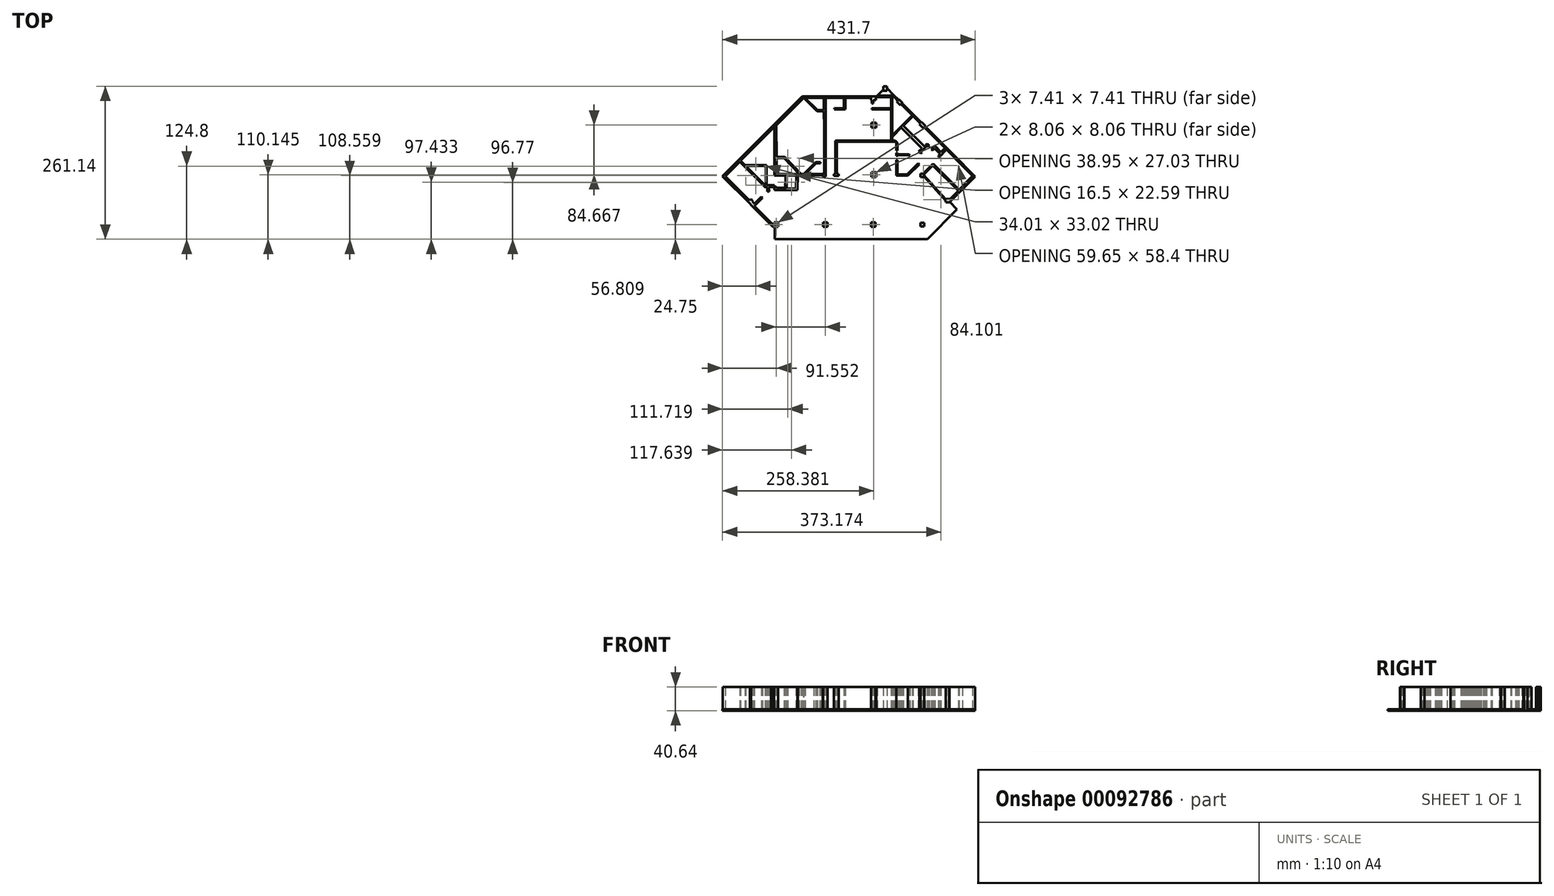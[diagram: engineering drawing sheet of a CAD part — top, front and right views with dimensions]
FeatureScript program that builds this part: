
annotation { "Feature Type Name" : "Feature", "Feature Type Description" : "" }
export const myFeature = defineFeature(function(context is Context, id is Id, definition is map)
    precondition{}
    {
        {
            var Q0;
            Q0=qCreatedBy(makeId("Top.planeOp"),FACE);
            var sketch = newSketch(context, id + "F0", { "sketchPlane" : qUnion([Q0])});
            skLineSegment(sketch, "E0", {"start": v(-215.85, -23.07) * mm, "end": v(-79.78, 113.2) * mm});
            skLineSegment(sketch, "E1", {"start": v(-79.78, 113.2) * mm, "end": v(46.96, 113.2) * mm});
            skLineSegment(sketch, "E2", {"start": v(46.96, 113.2) * mm, "end": v(58.85, 125.1) * mm});
            skLineSegment(sketch, "E3", {"start": v(58.85, 125.1) * mm, "end": v(58.85, 130.59) * mm});
            skLineSegment(sketch, "E4", {"start": v(58.85, 130.59) * mm, "end": v(65.02, 130.59) * mm});
            skLineSegment(sketch, "E5", {"start": v(65.02, 130.59) * mm, "end": v(65.02, 127.13) * mm});
            skLineSegment(sketch, "E6", {"start": v(65.02, 127.13) * mm, "end": v(84.8, 107.35) * mm});
            skLineSegment(sketch, "E7", {"start": v(84.8, 107.35) * mm, "end": v(85.59, 108.14) * mm});
            skLineSegment(sketch, "E8", {"start": v(85.59, 108.14) * mm, "end": v(91.7, 102.02) * mm});
            skLineSegment(sketch, "E9", {"start": v(91.7, 102.02) * mm, "end": v(90.95, 101.28) * mm});
            skLineSegment(sketch, "E10", {"start": v(90.95, 101.28) * mm, "end": v(123.63, 68.6) * mm});
            skLineSegment(sketch, "E11", {"start": v(123.63, 68.6) * mm, "end": v(124.34, 69.31) * mm});
            skLineSegment(sketch, "E12", {"start": v(124.34, 69.31) * mm, "end": v(130.43, 63.22) * mm});
            skLineSegment(sketch, "E13", {"start": v(130.43, 63.22) * mm, "end": v(129.76, 62.54) * mm});
            skLineSegment(sketch, "E14", {"start": v(129.76, 62.54) * mm, "end": v(215.85, -23.56) * mm});
            skLineSegment(sketch, "E15", {"start": v(215.85, -23.56) * mm, "end": v(172.3, -67.15) * mm});
            skLineSegment(sketch, "E16", {"start": v(172.3, -67.15) * mm, "end": v(184.3, -79.94) * mm});
            skLineSegment(sketch, "E17", {"start": v(184.3, -79.94) * mm, "end": v(134.66, -130.59) * mm});
            skLineSegment(sketch, "E18", {"start": v(134.66, -130.59) * mm, "end": v(-126.45, -130.35) * mm});
            skLineSegment(sketch, "E19", {"start": v(-126.45, -130.35) * mm, "end": v(-126.52, -109.63) * mm});
            skLineSegment(sketch, "E20", {"start": v(-126.52, -109.63) * mm, "end": v(-129.44, -109.56) * mm});
            skLineSegment(sketch, "E21", {"start": v(-129.44, -109.56) * mm, "end": v(-132.8, -106.33) * mm});
            skLineSegment(sketch, "E22", {"start": v(-132.8, -106.33) * mm, "end": v(-167.08, -72.04) * mm});
            skLineSegment(sketch, "E23", {"start": v(-167.08, -72.04) * mm, "end": v(-168.6, -70.28) * mm});
            skLineSegment(sketch, "E24", {"start": v(-168.6, -70.28) * mm, "end": v(-215.85, -23.07) * mm});
            skFitSpline(sketch, "E25", {"points": [v(-186.3, 1.77) * mm, v(-171.85, -12.85) * mm, v(-157.2, -27.26) * mm, v(-142.79, -41.93) * mm]});
            skLineSegment(sketch, "E26", {"start": v(-126.77, 61.2) * mm, "end": v(-126.8, -38.64) * mm});
            skLineSegment(sketch, "E27", {"start": v(-126.8, -38.64) * mm, "end": v(-140.51, -38.64) * mm});
            skLineSegment(sketch, "E28", {"start": v(-140.51, -38.64) * mm, "end": v(-140.51, -4.42) * mm});
            skLineSegment(sketch, "E29", {"start": v(-140.51, -4.42) * mm, "end": v(-177.03, -4.42) * mm});
            skLineSegment(sketch, "E30", {"start": v(-177.03, -4.42) * mm, "end": v(-184.77, 3.3) * mm});
            skLineSegment(sketch, "E31", {"start": v(-184.77, 3.3) * mm, "end": v(-186.3, 1.77) * mm});
            skFitSpline(sketch, "E32", {"points": [v(-56.02, -1.5) * mm, v(-56.02, -1.5) * mm, v(-50.03, -1.35) * mm, v(-49.46, -1.5) * mm, v(-56.02, -1.5) * mm]});
            skFitSpline(sketch, "E33", {"points": [v(-49.46, -1.5) * mm, v(-48.9, -1.64) * mm, v(-49.32, 0.79) * mm, v(-49.32, 0.79) * mm, v(-49.46, -1.5) * mm]});
            skLineSegment(sketch, "E34", {"start": v(-142.79, -41.93) * mm, "end": v(-139.28, -41.93) * mm});
            skLineSegment(sketch, "E35", {"start": v(-139.28, -41.93) * mm, "end": v(-139.29, -49.25) * mm});
            skLineSegment(sketch, "E36", {"start": v(-139.29, -49.25) * mm, "end": v(-136.12, -49.48) * mm});
            skLineSegment(sketch, "E37", {"start": v(-136.12, -49.48) * mm, "end": v(-136.52, -41.93) * mm});
            skLineSegment(sketch, "E38", {"start": v(-136.52, -41.93) * mm, "end": v(-126.8, -41.93) * mm});
            skLineSegment(sketch, "E39", {"start": v(-126.8, -41.93) * mm, "end": v(-126.8, -47.66) * mm});
            skLineSegment(sketch, "E40", {"start": v(-126.8, -47.66) * mm, "end": v(-123.39, -47.66) * mm});
            skLineSegment(sketch, "E41", {"start": v(-123.39, -47.66) * mm, "end": v(-123.39, -46.49) * mm});
            skLineSegment(sketch, "E42", {"start": v(-123.39, -46.49) * mm, "end": v(-87.44, -46.72) * mm});
            skLineSegment(sketch, "E43", {"start": v(-87.44, -46.72) * mm, "end": v(-86.94, -21.61) * mm});
            skLineSegment(sketch, "E44", {"start": v(-86.94, -21.61) * mm, "end": v(-44.03, -21.54) * mm});
            skLineSegment(sketch, "E45", {"start": v(-44.03, -21.54) * mm, "end": v(-44.76, -19.22) * mm});
            skLineSegment(sketch, "E46", {"start": v(-44.76, -19.22) * mm, "end": v(-74.5, -19.31) * mm});
            skLineSegment(sketch, "E47", {"start": v(-74.5, -19.31) * mm, "end": v(-56.02, -1.5) * mm});
            skLineSegment(sketch, "E48", {"start": v(-49.32, 0.79) * mm, "end": v(-55.87, 1.07) * mm});
            skLineSegment(sketch, "E49", {"start": v(-55.87, 1.07) * mm, "end": v(-76.69, -19.32) * mm});
            skLineSegment(sketch, "E50", {"start": v(-76.69, -19.32) * mm, "end": v(-81.21, -19.34) * mm});
            skLineSegment(sketch, "E51", {"start": v(-81.21, -19.34) * mm, "end": v(-109.05, 9.62) * mm});
            skLineSegment(sketch, "E52", {"start": v(-109.05, 9.62) * mm, "end": v(-123.39, 9.48) * mm});
            skLineSegment(sketch, "E53", {"start": v(-123.39, 9.48) * mm, "end": v(-123.39, 31.81) * mm});
            skLineSegment(sketch, "E54", {"start": v(-123.39, 31.81) * mm, "end": v(-123.46, 64.51) * mm});
            skLineSegment(sketch, "E55", {"start": v(-123.46, 64.51) * mm, "end": v(-126.77, 61.2) * mm});
            skLineSegment(sketch, "E56", {"start": v(-8.23, 111.03) * mm, "end": v(-8.44, 93.23) * mm});
            skLineSegment(sketch, "E57", {"start": v(-8.44, 93.23) * mm, "end": v(-24.56, 93.56) * mm});
            skLineSegment(sketch, "E58", {"start": v(-24.56, 93.56) * mm, "end": v(-24.7, 91.44) * mm});
            skLineSegment(sketch, "E59", {"start": v(-24.7, 91.44) * mm, "end": v(-6.21, 91.4) * mm});
            skLineSegment(sketch, "E60", {"start": v(-6.21, 91.4) * mm, "end": v(-5.91, 111.02) * mm});
            skLineSegment(sketch, "E61", {"start": v(-5.91, 111.02) * mm, "end": v(37.7, 110.88) * mm});
            skLineSegment(sketch, "E62", {"start": v(37.7, 110.88) * mm, "end": v(37.7, 107.03) * mm});
            skLineSegment(sketch, "E63", {"start": v(37.7, 107.03) * mm, "end": v(39.2, 107.03) * mm});
            skLineSegment(sketch, "E64", {"start": v(39.2, 107.03) * mm, "end": v(39.2, 101.13) * mm});
            skLineSegment(sketch, "E65", {"start": v(39.2, 101.13) * mm, "end": v(41.9, 101.13) * mm});
            skLineSegment(sketch, "E66", {"start": v(41.9, 101.13) * mm, "end": v(41.9, 107) * mm});
            skLineSegment(sketch, "E67", {"start": v(41.9, 107) * mm, "end": v(46.12, 106.98) * mm});
            skLineSegment(sketch, "E68", {"start": v(46.12, 106.98) * mm, "end": v(46.1, 111.97) * mm});
            skLineSegment(sketch, "E69", {"start": v(46.1, 111.97) * mm, "end": v(72.04, 112.1) * mm});
            skLineSegment(sketch, "E70", {"start": v(72.04, 112.1) * mm, "end": v(71.96, 93.06) * mm});
            skLineSegment(sketch, "E71", {"start": v(71.96, 93.06) * mm, "end": v(39.07, 93.1) * mm});
            skLineSegment(sketch, "E72", {"start": v(39.07, 93.1) * mm, "end": v(39.39, 91.15) * mm});
            skLineSegment(sketch, "E73", {"start": v(39.39, 91.15) * mm, "end": v(72.19, 91.01) * mm});
            skLineSegment(sketch, "E74", {"start": v(72.19, 91.01) * mm, "end": v(72.26, 80.52) * mm});
            skLineSegment(sketch, "E75", {"start": v(72.26, 80.52) * mm, "end": v(73.98, 80.49) * mm});
            skLineSegment(sketch, "E76", {"start": v(73.98, 80.49) * mm, "end": v(74.27, 112.15) * mm});
            skLineSegment(sketch, "E77", {"start": v(74.27, 112.15) * mm, "end": v(77.66, 112.2) * mm});
            skLineSegment(sketch, "E78", {"start": v(77.66, 112.2) * mm, "end": v(83.4, 105.92) * mm});
            skLineSegment(sketch, "E79", {"start": v(83.4, 105.92) * mm, "end": v(84.97, 107.56) * mm});
            skLineSegment(sketch, "E80", {"start": v(84.97, 107.56) * mm, "end": v(77.56, 114.78) * mm});
            skLineSegment(sketch, "E81", {"start": v(77.56, 114.78) * mm, "end": v(46.1, 114.8) * mm});
            skLineSegment(sketch, "E82", {"start": v(46.1, 114.8) * mm, "end": v(37.7, 114.8) * mm});
            skLineSegment(sketch, "E83", {"start": v(37.7, 114.8) * mm, "end": v(-78.2, 114.88) * mm});
            skLineSegment(sketch, "E84", {"start": v(-78.2, 114.88) * mm, "end": v(-215.75, -23.11) * mm});
            skLineSegment(sketch, "E85", {"start": v(-215.75, -23.11) * mm, "end": v(-169.21, -69.65) * mm});
            skLineSegment(sketch, "E86", {"start": v(-169.21, -69.65) * mm, "end": v(-169.36, -69.8) * mm});
            skLineSegment(sketch, "E87", {"start": v(-169.36, -69.8) * mm, "end": v(-129.37, -109.8) * mm});
            skLineSegment(sketch, "E88", {"start": v(-129.37, -109.8) * mm, "end": v(-126.86, -109.12) * mm});
            skLineSegment(sketch, "E89", {"start": v(-126.86, -109.12) * mm, "end": v(-126.86, -105.06) * mm});
            skLineSegment(sketch, "E90", {"start": v(-126.86, -105.06) * mm, "end": v(-130.35, -105.06) * mm});
            skLineSegment(sketch, "E91", {"start": v(-130.35, -105.06) * mm, "end": v(-161.43, -73.98) * mm});
            skLineSegment(sketch, "E92", {"start": v(-161.43, -73.98) * mm, "end": v(-147.4, -59.94) * mm});
            skLineSegment(sketch, "E93", {"start": v(-147.4, -59.94) * mm, "end": v(-149.1, -57.8) * mm});
            skLineSegment(sketch, "E94", {"start": v(-149.1, -57.8) * mm, "end": v(-161.22, -69.92) * mm});
            skLineSegment(sketch, "E95", {"start": v(-161.22, -69.92) * mm, "end": v(-164.83, -66.56) * mm});
            skLineSegment(sketch, "E96", {"start": v(-164.83, -66.56) * mm, "end": v(-163.73, -65.45) * mm});
            skLineSegment(sketch, "E97", {"start": v(-163.73, -65.45) * mm, "end": v(-167.29, -61.88) * mm});
            skLineSegment(sketch, "E98", {"start": v(-167.29, -61.88) * mm, "end": v(-169.86, -64.45) * mm});
            skLineSegment(sketch, "E99", {"start": v(-169.86, -64.45) * mm, "end": v(-211.2, -23.11) * mm});
            skLineSegment(sketch, "E100", {"start": v(-211.2, -23.11) * mm, "end": v(-76.8, 111.13) * mm});
            skLineSegment(sketch, "E101", {"start": v(-76.8, 111.13) * mm, "end": v(-8.23, 111.03) * mm});
            skFitSpline(sketch, "E102", {"points": [v(-42.68, 107.03) * mm, v(-42.64, 102.79) * mm, v(-42.66, 98.54) * mm, v(-42.8, 94.3) * mm]});
            skLineSegment(sketch, "E103", {"start": v(-45.39, 111.13) * mm, "end": v(-45.48, 107.13) * mm});
            skLineSegment(sketch, "E104", {"start": v(-45.48, 107.13) * mm, "end": v(-42.68, 107.03) * mm});
            skFitSpline(sketch, "E105", {"points": [v(-41.4, -20.44) * mm, v(-41.14, -22.5) * mm, v(-38.06, -19.94) * mm, v(-37.9, -21.46) * mm]});
            skFitSpline(sketch, "E106", {"points": [v(-37.9, -21.46) * mm, v(-37.4, -25.88) * mm, v(-38.04, -19.38) * mm, v(-38.04, -19.38) * mm, v(-37.9, -21.46) * mm]});
            skLineSegment(sketch, "E107", {"start": v(-42.8, 94.3) * mm, "end": v(-42.8, 65.7) * mm});
            skLineSegment(sketch, "E108", {"start": v(-42.8, 65.7) * mm, "end": v(-44.13, 65.7) * mm});
            skLineSegment(sketch, "E109", {"start": v(-44.13, 65.7) * mm, "end": v(-44.13, 60.85) * mm});
            skLineSegment(sketch, "E110", {"start": v(-44.13, 60.85) * mm, "end": v(-42.18, 60.85) * mm});
            skLineSegment(sketch, "E111", {"start": v(-42.18, 60.85) * mm, "end": v(-41.4, -20.44) * mm});
            skLineSegment(sketch, "E112", {"start": v(-38.04, -19.38) * mm, "end": v(-39.19, -19.31) * mm});
            skLineSegment(sketch, "E113", {"start": v(-39.19, -19.31) * mm, "end": v(-39.19, 60.64) * mm});
            skLineSegment(sketch, "E114", {"start": v(-39.19, 60.64) * mm, "end": v(-39.28, 62.96) * mm});
            skLineSegment(sketch, "E115", {"start": v(-39.28, 62.96) * mm, "end": v(-39.28, 65.7) * mm});
            skLineSegment(sketch, "E116", {"start": v(-39.28, 65.7) * mm, "end": v(-39.58, 65.7) * mm});
            skLineSegment(sketch, "E117", {"start": v(-39.58, 65.7) * mm, "end": v(-39.58, 90.87) * mm});
            skLineSegment(sketch, "E118", {"start": v(-39.58, 90.87) * mm, "end": v(-31.65, 90.87) * mm});
            skLineSegment(sketch, "E119", {"start": v(-31.65, 90.87) * mm, "end": v(-31.69, 93.32) * mm});
            skLineSegment(sketch, "E120", {"start": v(-31.69, 93.32) * mm, "end": v(-39.56, 93.3) * mm});
            skLineSegment(sketch, "E121", {"start": v(-39.56, 93.3) * mm, "end": v(-39.58, 107.03) * mm});
            skLineSegment(sketch, "E122", {"start": v(-39.58, 107.03) * mm, "end": v(-39.53, 111.09) * mm});
            skLineSegment(sketch, "E123", {"start": v(-39.53, 111.09) * mm, "end": v(-45.39, 111.13) * mm});
            skLineSegment(sketch, "E124", {"start": v(-110.62, 7.62) * mm, "end": v(-84.44, -19.35) * mm});
            skLineSegment(sketch, "E125", {"start": v(-84.44, -19.35) * mm, "end": v(-89, -19.37) * mm});
            skLineSegment(sketch, "E126", {"start": v(-89, -19.37) * mm, "end": v(-100.11, -19.4) * mm});
            skLineSegment(sketch, "E127", {"start": v(-100.11, -19.4) * mm, "end": v(-103.15, -19.4) * mm});
            skLineSegment(sketch, "E128", {"start": v(-103.15, -19.4) * mm, "end": v(-123.39, -19.4) * mm});
            skLineSegment(sketch, "E129", {"start": v(-123.39, -19.4) * mm, "end": v(-123.39, 7.49) * mm});
            skLineSegment(sketch, "E130", {"start": v(-123.39, 7.49) * mm, "end": v(-110.62, 7.62) * mm});
            skLineSegment(sketch, "E131", {"start": v(-175.83, -5.62) * mm, "end": v(-141.82, -5.62) * mm});
            skLineSegment(sketch, "E132", {"start": v(-141.82, -5.62) * mm, "end": v(-141.82, -38.64) * mm});
            skLineSegment(sketch, "E133", {"start": v(-141.82, -38.64) * mm, "end": v(-142.77, -38.64) * mm});
            skLineSegment(sketch, "E134", {"start": v(-142.77, -38.64) * mm, "end": v(-175.83, -5.62) * mm});
            skFitSpline(sketch, "E135", {"points": [v(-89.96, -44.54) * mm, v(-95.39, -44.46) * mm, v(-100.81, -44.51) * mm, v(-106.24, -44.55) * mm]});
            skLineSegment(sketch, "E136", {"start": v(-89.74, -21.97) * mm, "end": v(-89.96, -44.54) * mm});
            skLineSegment(sketch, "E137", {"start": v(-106.24, -44.55) * mm, "end": v(-106.13, -43.27) * mm});
            skLineSegment(sketch, "E138", {"start": v(-106.13, -43.27) * mm, "end": v(-106.13, -40.36) * mm});
            skLineSegment(sketch, "E139", {"start": v(-106.13, -40.36) * mm, "end": v(-106.13, -29.97) * mm});
            skLineSegment(sketch, "E140", {"start": v(-106.13, -29.97) * mm, "end": v(-106.13, -22.12) * mm});
            skLineSegment(sketch, "E141", {"start": v(-106.13, -22.12) * mm, "end": v(-104.14, -22.12) * mm});
            skLineSegment(sketch, "E142", {"start": v(-104.14, -22.12) * mm, "end": v(-89.74, -21.97) * mm});
            skLineSegment(sketch, "E143", {"start": v(-123.39, -22.12) * mm, "end": v(-108.2, -22.12) * mm});
            skLineSegment(sketch, "E144", {"start": v(-108.2, -22.12) * mm, "end": v(-108.2, -29.05) * mm});
            skLineSegment(sketch, "E145", {"start": v(-108.2, -29.05) * mm, "end": v(-108.41, -40.15) * mm});
            skLineSegment(sketch, "E146", {"start": v(-108.41, -40.15) * mm, "end": v(-108.38, -42.92) * mm});
            skLineSegment(sketch, "E147", {"start": v(-108.38, -42.92) * mm, "end": v(-123.39, -42.92) * mm});
            skLineSegment(sketch, "E148", {"start": v(-123.39, -42.92) * mm, "end": v(-123.39, -22.12) * mm});
            skLineSegment(sketch, "E149", {"start": v(-44.13, -19.12) * mm, "end": v(-39.28, -19.12) * mm});
            skLineSegment(sketch, "E150", {"start": v(-39.28, -19.12) * mm, "end": v(-39.28, -23.97) * mm});
            skLineSegment(sketch, "E151", {"start": v(-39.28, -23.97) * mm, "end": v(-44.13, -23.97) * mm});
            skLineSegment(sketch, "E152", {"start": v(-44.13, -23.97) * mm, "end": v(-44.13, -19.12) * mm});
            skLineSegment(sketch, "E153", {"start": v(90.99, 101.49) * mm, "end": v(89.12, 100.4) * mm});
            skLineSegment(sketch, "E154", {"start": v(89.12, 100.4) * mm, "end": v(108.5, 80.9) * mm});
            skLineSegment(sketch, "E155", {"start": v(108.5, 80.9) * mm, "end": v(75.07, 47.74) * mm});
            skLineSegment(sketch, "E156", {"start": v(75.07, 47.74) * mm, "end": v(75.12, 45.54) * mm});
            skLineSegment(sketch, "E157", {"start": v(75.12, 45.54) * mm, "end": v(89.59, 59.7) * mm});
            skLineSegment(sketch, "E158", {"start": v(89.59, 59.7) * mm, "end": v(124.84, 24.66) * mm});
            skLineSegment(sketch, "E159", {"start": v(124.84, 24.66) * mm, "end": v(119.4, 19.21) * mm});
            skLineSegment(sketch, "E160", {"start": v(119.4, 19.21) * mm, "end": v(122.82, 15.38) * mm});
            skLineSegment(sketch, "E161", {"start": v(122.82, 15.38) * mm, "end": v(124.63, 17) * mm});
            skLineSegment(sketch, "E162", {"start": v(124.63, 17) * mm, "end": v(122.82, 19.02) * mm});
            skLineSegment(sketch, "E163", {"start": v(122.82, 19.02) * mm, "end": v(133.5, 29.3) * mm});
            skLineSegment(sketch, "E164", {"start": v(133.5, 29.3) * mm, "end": v(135.52, 27.08) * mm});
            skLineSegment(sketch, "E165", {"start": v(135.52, 27.08) * mm, "end": v(137.33, 28.9) * mm});
            skLineSegment(sketch, "E166", {"start": v(137.33, 28.9) * mm, "end": v(134.1, 32.52) * mm});
            skLineSegment(sketch, "E167", {"start": v(134.1, 32.52) * mm, "end": v(129.07, 27.48) * mm});
            skLineSegment(sketch, "E168", {"start": v(129.07, 27.48) * mm, "end": v(93.04, 63.1) * mm});
            skLineSegment(sketch, "E169", {"start": v(93.04, 63.1) * mm, "end": v(109.8, 79.59) * mm});
            skLineSegment(sketch, "E170", {"start": v(109.8, 79.59) * mm, "end": v(122.15, 67.16) * mm});
            skLineSegment(sketch, "E171", {"start": v(122.15, 67.16) * mm, "end": v(120.57, 65.58) * mm});
            skLineSegment(sketch, "E172", {"start": v(120.57, 65.58) * mm, "end": v(126.7, 59.45) * mm});
            skLineSegment(sketch, "E173", {"start": v(126.7, 59.45) * mm, "end": v(128.26, 61.02) * mm});
            skLineSegment(sketch, "E174", {"start": v(128.26, 61.02) * mm, "end": v(159.59, 29.49) * mm});
            skLineSegment(sketch, "E175", {"start": v(159.59, 29.49) * mm, "end": v(164.15, 24.87) * mm});
            skLineSegment(sketch, "E176", {"start": v(164.15, 24.87) * mm, "end": v(157.3, 18.2) * mm});
            skLineSegment(sketch, "E177", {"start": v(157.3, 18.2) * mm, "end": v(147.42, 28.7) * mm});
            skLineSegment(sketch, "E178", {"start": v(147.42, 28.7) * mm, "end": v(140.96, 22.64) * mm});
            skLineSegment(sketch, "E179", {"start": v(140.96, 22.64) * mm, "end": v(143.18, 21.03) * mm});
            skLineSegment(sketch, "E180", {"start": v(143.18, 21.03) * mm, "end": v(146.8, 24.66) * mm});
            skLineSegment(sketch, "E181", {"start": v(146.8, 24.66) * mm, "end": v(155.88, 14.98) * mm});
            skLineSegment(sketch, "E182", {"start": v(155.88, 14.98) * mm, "end": v(152.86, 11.56) * mm});
            skLineSegment(sketch, "E183", {"start": v(152.86, 11.56) * mm, "end": v(154.27, 9.33) * mm});
            skLineSegment(sketch, "E184", {"start": v(154.27, 9.33) * mm, "end": v(166.67, 22.32) * mm});
            skLineSegment(sketch, "E185", {"start": v(166.67, 22.32) * mm, "end": v(193.9, -5.21) * mm});
            skLineSegment(sketch, "E186", {"start": v(193.9, -5.21) * mm, "end": v(198.22, -9.5) * mm});
            skLineSegment(sketch, "E187", {"start": v(198.22, -9.5) * mm, "end": v(211.45, -22.82) * mm});
            skLineSegment(sketch, "E188", {"start": v(211.45, -22.82) * mm, "end": v(188.53, -45.74) * mm});
            skLineSegment(sketch, "E189", {"start": v(188.53, -45.74) * mm, "end": v(143.82, -1.7) * mm});
            skLineSegment(sketch, "E190", {"start": v(143.82, -1.7) * mm, "end": v(124.93, -20.23) * mm});
            skLineSegment(sketch, "E191", {"start": v(124.93, -20.23) * mm, "end": v(165.64, -65.01) * mm});
            skLineSegment(sketch, "E192", {"start": v(165.64, -65.01) * mm, "end": v(165.64, -67.71) * mm});
            skLineSegment(sketch, "E193", {"start": v(165.64, -67.71) * mm, "end": v(171.29, -67.71) * mm});
            skLineSegment(sketch, "E194", {"start": v(171.29, -67.71) * mm, "end": v(171.41, -67.9) * mm});
            skLineSegment(sketch, "E195", {"start": v(171.41, -67.9) * mm, "end": v(171.6, -67.71) * mm});
            skLineSegment(sketch, "E196", {"start": v(171.6, -67.71) * mm, "end": v(171.62, -67.71) * mm});
            skLineSegment(sketch, "E197", {"start": v(171.62, -67.71) * mm, "end": v(171.62, -67.69) * mm});
            skLineSegment(sketch, "E198", {"start": v(171.62, -67.69) * mm, "end": v(215.8, -23.57) * mm});
            skLineSegment(sketch, "E199", {"start": v(215.8, -23.57) * mm, "end": v(129.82, 62.58) * mm});
            skLineSegment(sketch, "E200", {"start": v(129.82, 62.58) * mm, "end": v(130.5, 63.24) * mm});
            skLineSegment(sketch, "E201", {"start": v(130.5, 63.24) * mm, "end": v(124.35, 69.37) * mm});
            skLineSegment(sketch, "E202", {"start": v(124.35, 69.37) * mm, "end": v(123.7, 68.71) * mm});
            skLineSegment(sketch, "E203", {"start": v(123.7, 68.71) * mm, "end": v(90.99, 101.49) * mm});
            skLineSegment(sketch, "E204", {"start": v(143.45, -4.62) * mm, "end": v(187.15, -47.77) * mm});
            skLineSegment(sketch, "E205", {"start": v(187.15, -47.77) * mm, "end": v(171.62, -63.02) * mm});
            skLineSegment(sketch, "E206", {"start": v(171.62, -63.02) * mm, "end": v(171.62, -61.58) * mm});
            skLineSegment(sketch, "E207", {"start": v(171.62, -61.58) * mm, "end": v(165.64, -61.58) * mm});
            skLineSegment(sketch, "E208", {"start": v(165.64, -61.58) * mm, "end": v(165.64, -62.48) * mm});
            skLineSegment(sketch, "E209", {"start": v(165.64, -62.48) * mm, "end": v(127.5, -20.46) * mm});
            skLineSegment(sketch, "E210", {"start": v(127.5, -20.46) * mm, "end": v(143.45, -4.62) * mm});
            skLineSegment(sketch, "E211", {"start": v(38.5, 68.25) * mm, "end": v(46.56, 68.25) * mm});
            skLineSegment(sketch, "E212", {"start": v(46.56, 68.25) * mm, "end": v(46.56, 60.2) * mm});
            skLineSegment(sketch, "E213", {"start": v(46.56, 60.2) * mm, "end": v(38.5, 60.2) * mm});
            skLineSegment(sketch, "E214", {"start": v(38.5, 60.2) * mm, "end": v(38.5, 68.25) * mm});
            skLineSegment(sketch, "E215", {"start": v(38.5, -16.41) * mm, "end": v(46.56, -16.41) * mm});
            skLineSegment(sketch, "E216", {"start": v(46.56, -16.41) * mm, "end": v(46.56, -24.48) * mm});
            skLineSegment(sketch, "E217", {"start": v(46.56, -24.48) * mm, "end": v(38.5, -24.48) * mm});
            skLineSegment(sketch, "E218", {"start": v(38.5, -24.48) * mm, "end": v(38.5, -16.41) * mm});
            skLineSegment(sketch, "E219", {"start": v(85.58, 108.14) * mm, "end": v(91.71, 102.01) * mm});
            skLineSegment(sketch, "E220", {"start": v(91.71, 102.01) * mm, "end": v(87.93, 98.22) * mm});
            skLineSegment(sketch, "E221", {"start": v(87.93, 98.22) * mm, "end": v(81.8, 104.35) * mm});
            skLineSegment(sketch, "E222", {"start": v(81.8, 104.35) * mm, "end": v(85.58, 108.14) * mm});
            skLineSegment(sketch, "E223", {"start": v(58.79, 130.55) * mm, "end": v(65.06, 130.55) * mm});
            skLineSegment(sketch, "E224", {"start": v(65.06, 130.55) * mm, "end": v(65.06, 122.85) * mm});
            skLineSegment(sketch, "E225", {"start": v(65.06, 122.85) * mm, "end": v(58.79, 122.85) * mm});
            skLineSegment(sketch, "E226", {"start": v(58.79, 122.85) * mm, "end": v(58.79, 130.55) * mm});
            skLineSegment(sketch, "E227", {"start": v(-43.9, -102.13) * mm, "end": v(-36.5, -102.13) * mm});
            skLineSegment(sketch, "E228", {"start": v(-36.5, -102.13) * mm, "end": v(-36.5, -109.55) * mm});
            skLineSegment(sketch, "E229", {"start": v(-36.5, -109.55) * mm, "end": v(-43.9, -109.55) * mm});
            skLineSegment(sketch, "E230", {"start": v(-43.9, -109.55) * mm, "end": v(-43.9, -102.13) * mm});
            skLineSegment(sketch, "E231", {"start": v(37.92, -102.13) * mm, "end": v(45.33, -102.13) * mm});
            skLineSegment(sketch, "E232", {"start": v(45.33, -102.13) * mm, "end": v(45.33, -109.55) * mm});
            skLineSegment(sketch, "E233", {"start": v(45.33, -109.55) * mm, "end": v(37.92, -109.55) * mm});
            skLineSegment(sketch, "E234", {"start": v(37.92, -109.55) * mm, "end": v(37.92, -102.13) * mm});
            skLineSegment(sketch, "E235", {"start": v(-128, -102.13) * mm, "end": v(-120.6, -102.13) * mm});
            skLineSegment(sketch, "E236", {"start": v(-120.6, -102.13) * mm, "end": v(-120.6, -109.55) * mm});
            skLineSegment(sketch, "E237", {"start": v(-120.6, -109.55) * mm, "end": v(-128, -109.55) * mm});
            skLineSegment(sketch, "E238", {"start": v(-128, -109.55) * mm, "end": v(-128, -102.13) * mm});
            skLineSegment(sketch, "E239", {"start": v(122.45, -18.53) * mm, "end": v(128.43, -18.53) * mm});
            skLineSegment(sketch, "E240", {"start": v(128.43, -18.53) * mm, "end": v(128.43, -24.66) * mm});
            skLineSegment(sketch, "E241", {"start": v(128.43, -24.66) * mm, "end": v(122.45, -24.66) * mm});
            skLineSegment(sketch, "E242", {"start": v(122.45, -24.66) * mm, "end": v(122.45, -18.53) * mm});
            skLineSegment(sketch, "E243", {"start": v(122.45, -102.8) * mm, "end": v(128.43, -102.8) * mm});
            skLineSegment(sketch, "E244", {"start": v(128.43, -102.8) * mm, "end": v(128.43, -108.92) * mm});
            skLineSegment(sketch, "E245", {"start": v(128.43, -108.92) * mm, "end": v(122.45, -108.92) * mm});
            skLineSegment(sketch, "E246", {"start": v(122.45, -108.92) * mm, "end": v(122.45, -102.8) * mm});
            skFitSpline(sketch, "E247", {"points": [v(81.28, 35.54) * mm, v(81.67, 35.54) * mm, v(81.28, 22.99) * mm, v(81.28, 22.99) * mm, v(81.28, 35.54) * mm]});
            skLineSegment(sketch, "E248", {"start": v(72.22, 74.65) * mm, "end": v(72.22, 37.96) * mm});
            skLineSegment(sketch, "E249", {"start": v(72.22, 37.96) * mm, "end": v(-22.53, 37.96) * mm});
            skLineSegment(sketch, "E250", {"start": v(-22.53, 37.96) * mm, "end": v(-22.53, -19.08) * mm});
            skLineSegment(sketch, "E251", {"start": v(-22.53, -19.08) * mm, "end": v(-24.09, -19.08) * mm});
            skLineSegment(sketch, "E252", {"start": v(-24.09, -19.08) * mm, "end": v(-24.14, -21.71) * mm});
            skLineSegment(sketch, "E253", {"start": v(-24.14, -21.71) * mm, "end": v(-17.74, -21.71) * mm});
            skLineSegment(sketch, "E254", {"start": v(-17.74, -21.71) * mm, "end": v(-17.74, -19.08) * mm});
            skLineSegment(sketch, "E255", {"start": v(-17.74, -19.08) * mm, "end": v(-20.3, -19.08) * mm});
            skLineSegment(sketch, "E256", {"start": v(-20.3, -19.08) * mm, "end": v(-20.3, 35.54) * mm});
            skLineSegment(sketch, "E257", {"start": v(-20.3, 35.54) * mm, "end": v(81.28, 35.54) * mm});
            skFitSpline(sketch, "E258", {"points": [v(83.53, 12.76) * mm, v(83.53, 12.76) * mm, v(99.18, 12.86) * mm, v(104.5, 12.8) * mm, v(83.53, 12.76) * mm]});
            skLineSegment(sketch, "E259", {"start": v(81.28, 22.99) * mm, "end": v(83.3, 22.44) * mm});
            skLineSegment(sketch, "E260", {"start": v(83.3, 22.44) * mm, "end": v(83.3, 33.67) * mm});
            skLineSegment(sketch, "E261", {"start": v(83.3, 33.67) * mm, "end": v(102.82, 14.47) * mm});
            skLineSegment(sketch, "E262", {"start": v(102.82, 14.47) * mm, "end": v(83.68, 14.47) * mm});
            skLineSegment(sketch, "E263", {"start": v(83.68, 14.47) * mm, "end": v(83.68, 16.32) * mm});
            skLineSegment(sketch, "E264", {"start": v(83.68, 16.32) * mm, "end": v(81.82, 16.32) * mm});
            skLineSegment(sketch, "E265", {"start": v(81.82, 16.32) * mm, "end": v(81.82, 11.04) * mm});
            skLineSegment(sketch, "E266", {"start": v(81.82, 11.04) * mm, "end": v(83.53, 11.04) * mm});
            skLineSegment(sketch, "E267", {"start": v(83.53, 11.04) * mm, "end": v(83.53, 12.76) * mm});
            skLineSegment(sketch, "E268", {"start": v(104.5, 12.8) * mm, "end": v(118.67, -1.14) * mm});
            skLineSegment(sketch, "E269", {"start": v(118.67, -1.14) * mm, "end": v(99.48, -20.34) * mm});
            skLineSegment(sketch, "E270", {"start": v(99.48, -20.34) * mm, "end": v(83.5, -20.34) * mm});
            skLineSegment(sketch, "E271", {"start": v(83.5, -20.34) * mm, "end": v(83.5, 4.75) * mm});
            skLineSegment(sketch, "E272", {"start": v(83.5, 4.75) * mm, "end": v(81.3, 4.7) * mm});
            skLineSegment(sketch, "E273", {"start": v(81.3, 4.7) * mm, "end": v(81.3, -22.1) * mm});
            skLineSegment(sketch, "E274", {"start": v(81.3, -22.1) * mm, "end": v(101.05, -22.1) * mm});
            skLineSegment(sketch, "E275", {"start": v(101.05, -22.1) * mm, "end": v(132.8, 9.64) * mm});
            skLineSegment(sketch, "E276", {"start": v(132.8, 9.64) * mm, "end": v(129.48, 12.97) * mm});
            skLineSegment(sketch, "E277", {"start": v(129.48, 12.97) * mm, "end": v(126.85, 10.35) * mm});
            skLineSegment(sketch, "E278", {"start": v(126.85, 10.35) * mm, "end": v(128.95, 9.13) * mm});
            skLineSegment(sketch, "E279", {"start": v(128.95, 9.13) * mm, "end": v(120.1, 0.28) * mm});
            skLineSegment(sketch, "E280", {"start": v(120.1, 0.28) * mm, "end": v(75.12, 45.25) * mm});
            skLineSegment(sketch, "E281", {"start": v(75.12, 45.25) * mm, "end": v(75.04, 45.18) * mm});
            skLineSegment(sketch, "E282", {"start": v(75.04, 45.18) * mm, "end": v(75.04, 74.65) * mm});
            skLineSegment(sketch, "E283", {"start": v(75.04, 74.65) * mm, "end": v(72.22, 74.65) * mm});
            skLineSegment(sketch, "E284", {"start": v(75.04, 41.8) * mm, "end": v(79.36, 37.56) * mm});
            skLineSegment(sketch, "E285", {"start": v(79.36, 37.56) * mm, "end": v(75.04, 37.56) * mm});
            skLineSegment(sketch, "E286", {"start": v(75.04, 37.56) * mm, "end": v(75.04, 41.8) * mm});
            skLineSegment(sketch, "E287", {"start": v(-49.32, 89.73) * mm, "end": v(-49.32, 87.6) * mm});
            skLineSegment(sketch, "E288", {"start": v(-49.32, 87.6) * mm, "end": v(-53.74, 87.6) * mm});
            skLineSegment(sketch, "E289", {"start": v(-53.74, 87.6) * mm, "end": v(-76.79, 111) * mm});
            skLineSegment(sketch, "E290", {"start": v(-76.79, 111) * mm, "end": v(-74.76, 111.08) * mm});
            skLineSegment(sketch, "E291", {"start": v(-74.76, 111.08) * mm, "end": v(-53.38, 89.8) * mm});
            skLineSegment(sketch, "E292", {"start": v(-53.38, 89.8) * mm, "end": v(-49.32, 89.73) * mm});
            skLineSegment(sketch, "E293", {"start": v(-59.62, 93.4) * mm, "end": v(-81.8, 70.01) * mm});
            skLineSegment(sketch, "E294", {"start": v(-81.8, 70.01) * mm, "end": v(-81.8, 20.02) * mm});
            skLineSegment(sketch, "E295", {"start": v(-81.8, 20.02) * mm, "end": v(-59.11, -2.66) * mm});
            skLineSegment(sketch, "E296", {"start": v(-59.11, -2.66) * mm, "end": v(-67.68, -11.22) * mm});
            skLineSegment(sketch, "E297", {"start": v(-67.68, -11.22) * mm, "end": v(-94.8, 15.89) * mm});
            skLineSegment(sketch, "E298", {"start": v(-94.8, 15.89) * mm, "end": v(-94.8, 74.65) * mm});
            skLineSegment(sketch, "E299", {"start": v(-94.8, 74.65) * mm, "end": v(-67.37, 101) * mm});
            skLineSegment(sketch, "E300", {"start": v(-67.37, 101) * mm, "end": v(-59.62, 93.4) * mm});
            skSolve(sketch);
        }
        {
            var Q0;
            {var subQ26=sQuery(id+"F0.wireOp",EDGE,"E1");Q0=makeQuery(id+"F0.imprint","IMPRINT",FACE,{"disambiguationData":[TD([[makeQuery(id+"F0.imprint","IMPRINT",EDGE,{"derivedFrom":subQ26}),-1.0]])]});}
            var Q1;
            {var subQ16=sQuery(id+"F0.wireOp",EDGE,"E11");Q1=makeQuery(id+"F0.imprint","IMPRINT",FACE,{"disambiguationData":[TD([[makeQuery(id+"F0.imprint","IMPRINT",EDGE,{"derivedFrom":subQ16}),-1.0]])]});}
            var Q2;
            Q2=makeQuery(id+"F0.imprint","IMPRINT",FACE,{"disambiguationData":[TD([[makeQuery(id+"F0.imprint","IMPRINT",EDGE,{"derivedFrom":sQuery(id+"F0.wireOp",EDGE,"E211")}),-1.0]])]});
            var Q3;
            Q3=makeQuery(id+"F0.imprint","IMPRINT",FACE,{"disambiguationData":[TD([[makeQuery(id+"F0.imprint","IMPRINT",EDGE,{"derivedFrom":sQuery(id+"F0.wireOp",EDGE,"E215")}),-1.0]])]});
            var Q4;
            {var subQ2=sQuery(id+"F0.wireOp",EDGE,"E89");Q4=makeQuery(id+"F0.imprint","IMPRINT",FACE,{"disambiguationData":[TD([[makeQuery(id+"F0.imprint","IMPRINT",EDGE,{"derivedFrom":subQ2}),-1.0]])]});}
            var Q5;
            Q5=makeQuery(id+"F0.imprint","IMPRINT",FACE,{"disambiguationData":[TD([[makeQuery(id+"F0.imprint","IMPRINT",EDGE,{"derivedFrom":sQuery(id+"F0.wireOp",EDGE,"E227")}),-1.0]])]});
            var Q6;
            Q6=makeQuery(id+"F0.imprint","IMPRINT",FACE,{"disambiguationData":[TD([[makeQuery(id+"F0.imprint","IMPRINT",EDGE,{"derivedFrom":sQuery(id+"F0.wireOp",EDGE,"E231")}),-1.0]])]});
            var Q7;
            Q7=makeQuery(id+"F0.imprint","IMPRINT",FACE,{"disambiguationData":[TD([[makeQuery(id+"F0.imprint","IMPRINT",EDGE,{"derivedFrom":sQuery(id+"F0.wireOp",EDGE,"E243")}),-1.0]])]});
            var Q8;
            {var subQ0=sQuery(id+"F0.wireOp",EDGE,"E241");Q8=makeQuery(id+"F0.imprint","IMPRINT",FACE,{"disambiguationData":[TD([[makeQuery(id+"F0.imprint","IMPRINT",EDGE,{"derivedFrom":subQ0}),-1.0]])]});}
            var Q9;
            {var subQ5=sQuery(id+"F0.wireOp",EDGE,"E191");var subQ6=sQuery(id+"F0.wireOp",EDGE,"E190");var subQ7=makeQuery(id+"F0.imprint","INTERSECT",VERTEX,{"derivedFrom":[subQ6,subQ5]});Q9=makeQuery(id+"F0.imprint","IMPRINT",FACE,{"disambiguationData":[TD([[makeQuery(id+"F0.imprint","IMPRINT",EDGE,{"disambiguationData":[TD([[subQ7,1.0]])],"derivedFrom":subQ6}),1.0]])]});}
            var Q10;
            {var subQ9=sQuery(id+"F0.wireOp",EDGE,"E7");Q10=makeQuery(id+"F0.imprint","IMPRINT",FACE,{"disambiguationData":[TD([[makeQuery(id+"F0.imprint","IMPRINT",EDGE,{"derivedFrom":subQ9}),-1.0]])]});}
            var Q11;
            {var subQ13=sQuery(id+"F0.wireOp",EDGE,"E225");Q11=makeQuery(id+"F0.imprint","IMPRINT",FACE,{"disambiguationData":[TD([[makeQuery(id+"F0.imprint","IMPRINT",EDGE,{"derivedFrom":subQ13}),-1.0]])]});}
            extrude(context, id + "F1", {"entities" : qUnion([Q0, Q1, Q2, Q3, Q4, Q5, Q6, Q7, Q8, Q9, Q10, Q11]), "depth" : 40.64 * mm});
        }
        {
            var Q0;
            Q0=qCreatedBy(makeId("Top.planeOp"),FACE);
            var sketch = newSketch(context, id + "F2", { "sketchPlane" : qUnion([Q0])});
            skFitSpline(sketch, "E301", {"points": [v(-186.52, 1.87) * mm, v(-172.07, -12.75) * mm, v(-157.41, -27.16) * mm, v(-143, -41.82) * mm]});
            skLineSegment(sketch, "E302", {"start": v(-127.03, -38.54) * mm, "end": v(-140.73, -38.54) * mm});
            skLineSegment(sketch, "E303", {"start": v(-140.73, -38.54) * mm, "end": v(-140.73, -4.31) * mm});
            skLineSegment(sketch, "E304", {"start": v(-140.73, -4.31) * mm, "end": v(-177.25, -4.31) * mm});
            skLineSegment(sketch, "E305", {"start": v(-177.25, -4.31) * mm, "end": v(-184.99, 3.41) * mm});
            skLineSegment(sketch, "E306", {"start": v(-184.99, 3.41) * mm, "end": v(-186.52, 1.87) * mm});
            skLineSegment(sketch, "E307", {"start": v(-143, -41.82) * mm, "end": v(-139.5, -41.83) * mm});
            skLineSegment(sketch, "E308", {"start": v(-139.5, -41.83) * mm, "end": v(-139.5, -49.14) * mm});
            skLineSegment(sketch, "E309", {"start": v(-139.5, -49.14) * mm, "end": v(-136.34, -49.38) * mm});
            skLineSegment(sketch, "E310", {"start": v(-136.34, -49.38) * mm, "end": v(-136.74, -41.82) * mm});
            skLineSegment(sketch, "E311", {"start": v(-136.74, -41.82) * mm, "end": v(-127.03, -41.82) * mm});
            skLineSegment(sketch, "E312", {"start": v(-123.6, -46.38) * mm, "end": v(-87.66, -46.62) * mm});
            skLineSegment(sketch, "E313", {"start": v(-87.66, -46.62) * mm, "end": v(-87.16, -21.51) * mm});
            skLineSegment(sketch, "E314", {"start": v(-87.16, -21.51) * mm, "end": v(-44.25, -21.44) * mm});
            skLineSegment(sketch, "E315", {"start": v(-44.25, -21.44) * mm, "end": v(-44.98, -19.11) * mm});
            skLineSegment(sketch, "E316", {"start": v(-44.98, -19.11) * mm, "end": v(-74.7, -19.2) * mm});
            skLineSegment(sketch, "E317", {"start": v(-59.61, -2.27) * mm, "end": v(-76.9, -19.22) * mm});
            skLineSegment(sketch, "E318", {"start": v(-76.9, -19.22) * mm, "end": v(-81.43, -19.24) * mm});
            skLineSegment(sketch, "E319", {"start": v(-81.43, -19.24) * mm, "end": v(-109.26, 9.73) * mm});
            skLineSegment(sketch, "E320", {"start": v(-109.26, 9.73) * mm, "end": v(-123.6, 9.59) * mm});
            skLineSegment(sketch, "E321", {"start": v(-186.51, 1.86) * mm, "end": v(-184.97, 3.4) * mm});
            skLineSegment(sketch, "E322", {"start": v(-43.01, 89.83) * mm, "end": v(-43.01, 87.7) * mm});
            skLineSegment(sketch, "E323", {"start": v(-110.83, 7.73) * mm, "end": v(-84.66, -19.24) * mm});
            skLineSegment(sketch, "E324", {"start": v(-84.66, -19.24) * mm, "end": v(-89.23, -19.26) * mm});
            skLineSegment(sketch, "E325", {"start": v(-89.23, -19.26) * mm, "end": v(-100.33, -19.3) * mm});
            skLineSegment(sketch, "E326", {"start": v(-100.33, -19.3) * mm, "end": v(-103.36, -19.3) * mm});
            skLineSegment(sketch, "E327", {"start": v(-103.36, -19.3) * mm, "end": v(-123.6, -19.3) * mm});
            skLineSegment(sketch, "E328", {"start": v(-123.6, 7.6) * mm, "end": v(-110.83, 7.73) * mm});
            skLineSegment(sketch, "E329", {"start": v(-176.04, -5.52) * mm, "end": v(-142.04, -5.52) * mm});
            skLineSegment(sketch, "E330", {"start": v(-142.04, -5.52) * mm, "end": v(-142.04, -38.54) * mm});
            skLineSegment(sketch, "E331", {"start": v(-142.04, -38.54) * mm, "end": v(-142.99, -38.54) * mm});
            skLineSegment(sketch, "E332", {"start": v(-142.99, -38.54) * mm, "end": v(-176.04, -5.52) * mm});
            skFitSpline(sketch, "E333", {"points": [v(-90.18, -44.44) * mm, v(-95.6, -44.35) * mm, v(-101.03, -44.41) * mm, v(-106.46, -44.45) * mm]});
            skLineSegment(sketch, "E334", {"start": v(-89.96, -21.86) * mm, "end": v(-90.18, -44.44) * mm});
            skLineSegment(sketch, "E335", {"start": v(-106.46, -44.45) * mm, "end": v(-106.35, -43.16) * mm});
            skLineSegment(sketch, "E336", {"start": v(-106.35, -43.16) * mm, "end": v(-106.35, -40.25) * mm});
            skLineSegment(sketch, "E337", {"start": v(-106.35, -40.25) * mm, "end": v(-106.35, -29.86) * mm});
            skLineSegment(sketch, "E338", {"start": v(-106.35, -29.86) * mm, "end": v(-106.35, -22.01) * mm});
            skLineSegment(sketch, "E339", {"start": v(-106.35, -22.01) * mm, "end": v(-104.36, -22.01) * mm});
            skLineSegment(sketch, "E340", {"start": v(-104.36, -22.01) * mm, "end": v(-89.96, -21.86) * mm});
            skLineSegment(sketch, "E341", {"start": v(-123.6, -22.01) * mm, "end": v(-108.42, -22.01) * mm});
            skLineSegment(sketch, "E342", {"start": v(-108.42, -22.01) * mm, "end": v(-108.42, -28.95) * mm});
            skLineSegment(sketch, "E343", {"start": v(-108.42, -28.95) * mm, "end": v(-108.63, -40.05) * mm});
            skLineSegment(sketch, "E344", {"start": v(-108.63, -40.05) * mm, "end": v(-108.6, -42.82) * mm});
            skLineSegment(sketch, "E345", {"start": v(-108.6, -42.82) * mm, "end": v(-123.6, -42.82) * mm});
            skLineSegment(sketch, "E346", {"start": v(-44.35, -19.02) * mm, "end": v(-42.4, -19.02) * mm});
            skLineSegment(sketch, "E347", {"start": v(-39.5, -19.02) * mm, "end": v(-39.5, -23.87) * mm});
            skLineSegment(sketch, "E348", {"start": v(-39.5, -23.86) * mm, "end": v(-44.35, -23.86) * mm});
            skLineSegment(sketch, "E349", {"start": v(-44.35, -23.86) * mm, "end": v(-44.35, -19.02) * mm});
            skLineSegment(sketch, "E350", {"start": v(159.37, 29.59) * mm, "end": v(163.93, 24.98) * mm});
            skLineSegment(sketch, "E351", {"start": v(163.93, 24.98) * mm, "end": v(157.07, 18.3) * mm});
            skLineSegment(sketch, "E352", {"start": v(157.07, 18.3) * mm, "end": v(147.2, 28.8) * mm});
            skLineSegment(sketch, "E353", {"start": v(147.2, 28.8) * mm, "end": v(140.74, 22.75) * mm});
            skLineSegment(sketch, "E354", {"start": v(140.74, 22.75) * mm, "end": v(142.96, 21.13) * mm});
            skLineSegment(sketch, "E355", {"start": v(142.96, 21.13) * mm, "end": v(146.59, 24.76) * mm});
            skLineSegment(sketch, "E356", {"start": v(146.59, 24.76) * mm, "end": v(155.66, 15.08) * mm});
            skLineSegment(sketch, "E357", {"start": v(155.66, 15.08) * mm, "end": v(152.64, 11.66) * mm});
            skLineSegment(sketch, "E358", {"start": v(152.64, 11.66) * mm, "end": v(154.05, 9.44) * mm});
            skLineSegment(sketch, "E359", {"start": v(154.05, 9.44) * mm, "end": v(166.45, 22.43) * mm});
            skLineSegment(sketch, "E360", {"start": v(166.45, 22.43) * mm, "end": v(193.68, -5.1) * mm});
            skLineSegment(sketch, "E361", {"start": v(193.68, -5.1) * mm, "end": v(198, -9.4) * mm});
            skLineSegment(sketch, "E362", {"start": v(198, -9.4) * mm, "end": v(211.23, -22.72) * mm});
            skLineSegment(sketch, "E363", {"start": v(211.23, -22.72) * mm, "end": v(188.31, -45.64) * mm});
            skLineSegment(sketch, "E364", {"start": v(188.31, -45.64) * mm, "end": v(143.6, -1.59) * mm});
            skLineSegment(sketch, "E365", {"start": v(143.6, -1.59) * mm, "end": v(124.7, -20.13) * mm});
            skLineSegment(sketch, "E366", {"start": v(124.7, -20.13) * mm, "end": v(165.42, -64.91) * mm});
            skLineSegment(sketch, "E367", {"start": v(165.42, -64.91) * mm, "end": v(165.42, -67.61) * mm});
            skLineSegment(sketch, "E368", {"start": v(165.42, -67.61) * mm, "end": v(171.07, -67.61) * mm});
            skLineSegment(sketch, "E369", {"start": v(171.07, -67.61) * mm, "end": v(171.2, -67.8) * mm});
            skLineSegment(sketch, "E370", {"start": v(171.2, -67.8) * mm, "end": v(171.38, -67.61) * mm});
            skLineSegment(sketch, "E371", {"start": v(171.38, -67.61) * mm, "end": v(171.4, -67.61) * mm});
            skLineSegment(sketch, "E372", {"start": v(171.4, -67.61) * mm, "end": v(171.4, -67.58) * mm});
            skLineSegment(sketch, "E373", {"start": v(171.4, -67.58) * mm, "end": v(215.57, -23.47) * mm});
            skLineSegment(sketch, "E374", {"start": v(143.23, -4.52) * mm, "end": v(186.93, -47.67) * mm});
            skLineSegment(sketch, "E375", {"start": v(186.93, -47.67) * mm, "end": v(171.4, -62.92) * mm});
            skLineSegment(sketch, "E376", {"start": v(171.4, -62.92) * mm, "end": v(171.4, -61.48) * mm});
            skLineSegment(sketch, "E377", {"start": v(171.4, -61.48) * mm, "end": v(165.42, -61.48) * mm});
            skLineSegment(sketch, "E378", {"start": v(165.42, -61.48) * mm, "end": v(165.42, -62.38) * mm});
            skLineSegment(sketch, "E379", {"start": v(165.42, -62.38) * mm, "end": v(127.28, -20.36) * mm});
            skLineSegment(sketch, "E380", {"start": v(127.28, -20.36) * mm, "end": v(143.23, -4.52) * mm});
            skLineSegment(sketch, "E381", {"start": v(122.23, -18.43) * mm, "end": v(128.21, -18.43) * mm});
            skLineSegment(sketch, "E382", {"start": v(128.21, -18.43) * mm, "end": v(128.21, -24.56) * mm});
            skLineSegment(sketch, "E383", {"start": v(128.21, -24.56) * mm, "end": v(122.23, -24.56) * mm});
            skLineSegment(sketch, "E384", {"start": v(122.23, -24.56) * mm, "end": v(122.23, -18.43) * mm});
            skLineSegment(sketch, "E385", {"start": v(72, 38.06) * mm, "end": v(-22.75, 38.06) * mm});
            skLineSegment(sketch, "E386", {"start": v(-20.52, 35.65) * mm, "end": v(81.06, 35.65) * mm});
            skLineSegment(sketch, "E387", {"start": v(83.09, 33.77) * mm, "end": v(102.6, 14.57) * mm});
            skLineSegment(sketch, "E388", {"start": v(104.28, 12.91) * mm, "end": v(118.45, -1.04) * mm});
            skLineSegment(sketch, "E389", {"start": v(118.45, -1.04) * mm, "end": v(99.26, -20.23) * mm});
            skLineSegment(sketch, "E390", {"start": v(99.26, -20.23) * mm, "end": v(83.3, -20.23) * mm});
            skLineSegment(sketch, "E391", {"start": v(83.3, -20.23) * mm, "end": v(83.3, 4.85) * mm});
            skLineSegment(sketch, "E392", {"start": v(83.3, 4.85) * mm, "end": v(81.08, 4.8) * mm});
            skLineSegment(sketch, "E393", {"start": v(81.08, 4.8) * mm, "end": v(81.08, -22) * mm});
            skLineSegment(sketch, "E394", {"start": v(81.08, -22) * mm, "end": v(100.83, -22) * mm});
            skLineSegment(sketch, "E395", {"start": v(74.9, 45.36) * mm, "end": v(74.82, 45.28) * mm});
            skLineSegment(sketch, "E396", {"start": v(-49.54, 87.7) * mm, "end": v(-53.96, 87.7) * mm});
            skLineSegment(sketch, "E397", {"start": v(-53.96, 87.7) * mm, "end": v(-77, 111.1) * mm});
            skLineSegment(sketch, "E398", {"start": v(-77, 111.1) * mm, "end": v(-74.98, 111.18) * mm});
            skLineSegment(sketch, "E399", {"start": v(-74.98, 111.18) * mm, "end": v(-53.6, 89.9) * mm});
            skLineSegment(sketch, "E400", {"start": v(-53.6, 89.9) * mm, "end": v(-49.54, 89.83) * mm});
            skLineSegment(sketch, "E401", {"start": v(-59.83, 93.5) * mm, "end": v(-82, 70.12) * mm});
            skLineSegment(sketch, "E402", {"start": v(-82, 70.12) * mm, "end": v(-82, 20.12) * mm});
            skLineSegment(sketch, "E403", {"start": v(-82, 20.12) * mm, "end": v(-59.61, -2.27) * mm});
            skLineSegment(sketch, "E404", {"start": v(-68.27, -10.75) * mm, "end": v(-95.01, 16) * mm});
            skLineSegment(sketch, "E405", {"start": v(-95.01, 16) * mm, "end": v(-95.01, 74.75) * mm});
            skLineSegment(sketch, "E406", {"start": v(-95.01, 74.75) * mm, "end": v(-67.59, 101.11) * mm});
            skLineSegment(sketch, "E407", {"start": v(-67.59, 101.11) * mm, "end": v(-59.83, 93.5) * mm});
            skLineSegment(sketch, "E408", {"start": v(-184.97, 3.4) * mm, "end": v(-186.51, 1.86) * mm});
            skLineSegment(sketch, "E409", {"start": v(-186.51, 1.86) * mm, "end": v(-143, -41.82) * mm});
            skLineSegment(sketch, "E410", {"start": v(-143, -41.82) * mm, "end": v(-142.99, -38.54) * mm});
            skLineSegment(sketch, "E411", {"start": v(-142.99, -38.54) * mm, "end": v(-184.97, 3.4) * mm});
            skLineSegment(sketch, "E412", {"start": v(-142.04, -38.54) * mm, "end": v(-140.73, -38.54) * mm});
            skLineSegment(sketch, "E413", {"start": v(-139.5, -41.83) * mm, "end": v(-136.74, -41.82) * mm});
            skLineSegment(sketch, "E414", {"start": v(-127.03, -41.82) * mm, "end": v(-127.03, -38.54) * mm});
            skLineSegment(sketch, "E415", {"start": v(-123.6, 9.59) * mm, "end": v(-123.6, 7.6) * mm});
            skLineSegment(sketch, "E416", {"start": v(-123.6, -19.3) * mm, "end": v(-123.6, -22.01) * mm});
            skLineSegment(sketch, "E417", {"start": v(-123.6, -42.82) * mm, "end": v(-123.6, -46.38) * mm});
            skLineSegment(sketch, "E418", {"start": v(-84.66, -19.24) * mm, "end": v(-81.43, -19.24) * mm});
            skLineSegment(sketch, "E419", {"start": v(-108.42, -22.01) * mm, "end": v(-106.35, -22.01) * mm});
            skLineSegment(sketch, "E420", {"start": v(-89.96, -21.86) * mm, "end": v(-87.16, -21.51) * mm});
            skLineSegment(sketch, "E421", {"start": v(-76.9, -19.22) * mm, "end": v(-74.7, -19.2) * mm});
            skLineSegment(sketch, "E422", {"start": v(-59.61, -2.27) * mm, "end": v(-56.5, 0.83) * mm});
            skLineSegment(sketch, "E423", {"start": v(-56.5, 0.83) * mm, "end": v(-48.34, 0.83) * mm});
            skPoint(sketch, "E424.end.orphan", {"position": v(-48.34, 0) * mm});
            skLineSegment(sketch, "E425", {"start": v(-48.34, 0.83) * mm, "end": v(-48.34, 0) * mm});
            skLineSegment(sketch, "E426", {"start": v(-48.34, 0) * mm, "end": v(-48.34, -0.8) * mm});
            skLineSegment(sketch, "E427", {"start": v(-48.34, -0.8) * mm, "end": v(-56, -0.8) * mm});
            skLineSegment(sketch, "E428", {"start": v(-56, -0.8) * mm, "end": v(-74.7, -19.2) * mm});
            skLineSegment(sketch, "E429", {"start": v(-49.54, 89.83) * mm, "end": v(-43.01, 89.83) * mm});
            skLineSegment(sketch, "E430", {"start": v(-43.01, 87.7) * mm, "end": v(-49.54, 87.7) * mm});
            skLineSegment(sketch, "E431", {"start": v(-42.4, -19.02) * mm, "end": v(-39.5, -19.02) * mm});
            skLineSegment(sketch, "E432", {"start": v(-42.4, 60.94) * mm, "end": v(-39.8, 60.94) * mm});
            skLineSegment(sketch, "E433", {"start": v(-39.8, 60.94) * mm, "end": v(-39.5, -19.02) * mm});
            skLineSegment(sketch, "E434", {"start": v(-42.4, -19.02) * mm, "end": v(-42.4, 60.94) * mm});
            skLineSegment(sketch, "E435", {"start": v(-42.4, 60.94) * mm, "end": v(-43.01, 87.7) * mm});
            skLineSegment(sketch, "E436", {"start": v(-43.01, 89.83) * mm, "end": v(-43.01, 110.92) * mm});
            skLineSegment(sketch, "E437", {"start": v(-43.01, 110.92) * mm, "end": v(-39.67, 110.92) * mm});
            skLineSegment(sketch, "E438", {"start": v(-39.67, 110.92) * mm, "end": v(-39.8, 60.94) * mm});
            skLineSegment(sketch, "E439", {"start": v(79.14, 37.66) * mm, "end": v(81.06, 35.65) * mm});
            skLineSegment(sketch, "E440.bottom", {"start": v(-25.64, -19.58) * mm, "end": v(-17.47, -19.58) * mm});
            skLineSegment(sketch, "E440.top", {"start": v(-25.64, -22.8) * mm, "end": v(-17.47, -22.8) * mm});
            skLineSegment(sketch, "E440.left", {"start": v(-25.64, -19.58) * mm, "end": v(-25.64, -22.8) * mm});
            skLineSegment(sketch, "E440.right", {"start": v(-17.47, -19.58) * mm, "end": v(-17.47, -22.8) * mm});
            skLineSegment(sketch, "E441", {"start": v(72, 38.06) * mm, "end": v(74.82, 37.66) * mm});
            skLineSegment(sketch, "E442", {"start": v(74.82, 37.66) * mm, "end": v(79.14, 37.66) * mm});
            skLineSegment(sketch, "E443", {"start": v(-22.75, 38.06) * mm, "end": v(-22.75, -19.58) * mm});
            skPoint(sketch, "E443.endSnap0", {"position": v(-21.55, -19.58) * mm});
            skLineSegment(sketch, "E444", {"start": v(-20.52, 35.65) * mm, "end": v(-20.52, -19.58) * mm});
            skLineSegment(sketch, "E445", {"start": v(-20.52, -19.58) * mm, "end": v(-22.75, -19.58) * mm});
            skLineSegment(sketch, "E446", {"start": v(72, 80.47) * mm, "end": v(72, 38.06) * mm});
            skLineSegment(sketch, "E447", {"start": v(72, 80.47) * mm, "end": v(73.98, 80.47) * mm});
            skLineSegment(sketch, "E448", {"start": v(73.98, 80.47) * mm, "end": v(73.98, 37.86) * mm});
            skPoint(sketch, "E448.endSnap0", {"position": v(73.41, 37.86) * mm});
            skLineSegment(sketch, "E449", {"start": v(73.98, 37.86) * mm, "end": v(72, 38.06) * mm});
            skLineSegment(sketch, "E450", {"start": v(102.6, 14.57) * mm, "end": v(83.09, 14.57) * mm});
            skLineSegment(sketch, "E451", {"start": v(83.09, 14.57) * mm, "end": v(83.09, 16.65) * mm});
            skLineSegment(sketch, "E452", {"start": v(83.09, 16.65) * mm, "end": v(81.06, 16.65) * mm});
            skLineSegment(sketch, "E453", {"start": v(81.06, 16.65) * mm, "end": v(81.08, 11.76) * mm});
            skLineSegment(sketch, "E454", {"start": v(81.08, 11.76) * mm, "end": v(83.43, 11.77) * mm});
            skLineSegment(sketch, "E455", {"start": v(83.43, 11.77) * mm, "end": v(83.43, 12.91) * mm});
            skLineSegment(sketch, "E456", {"start": v(83.43, 12.91) * mm, "end": v(104.42, 12.94) * mm});
            skLineSegment(sketch, "E457", {"start": v(104.42, 12.94) * mm, "end": v(102.6, 14.57) * mm});
            skLineSegment(sketch, "E458", {"start": v(100.83, -22) * mm, "end": v(120.19, -2.65) * mm});
            skLineSegment(sketch, "E459", {"start": v(120.19, -2.65) * mm, "end": v(118.45, -1.04) * mm});
            skLineSegment(sketch, "E460", {"start": v(81.06, 35.65) * mm, "end": v(81.06, 20.48) * mm});
            skLineSegment(sketch, "E461", {"start": v(81.06, 20.48) * mm, "end": v(83.09, 20.48) * mm});
            skLineSegment(sketch, "E462", {"start": v(83.09, 20.48) * mm, "end": v(83.09, 33.77) * mm});
            skLineSegment(sketch, "E463", {"start": v(83.09, 33.77) * mm, "end": v(81.06, 35.65) * mm});
            skLineSegment(sketch, "E464", {"start": v(120.19, -2.65) * mm, "end": v(121.98, -0.86) * mm});
            skLineSegment(sketch, "E465", {"start": v(121.98, -0.86) * mm, "end": v(83.05, 38.06) * mm});
            skLineSegment(sketch, "E466", {"start": v(83.05, 38.06) * mm, "end": v(79.14, 37.66) * mm});
            skLineSegment(sketch, "E467", {"start": v(-123.6, -46.38) * mm, "end": v(-127.03, -46.36) * mm});
            skLineSegment(sketch, "E468", {"start": v(-127.03, -46.36) * mm, "end": v(-127.03, -41.82) * mm});
            skLineSegment(sketch, "E469", {"start": v(-123.6, -41.82) * mm, "end": v(-123.6, -42.82) * mm});
            skLineSegment(sketch, "E470", {"start": v(-123.6, -41.82) * mm, "end": v(-127.03, -41.82) * mm});
            skLineSegment(sketch, "E471", {"start": v(-123.6, -22.01) * mm, "end": v(-127.03, -22.01) * mm});
            skLineSegment(sketch, "E472", {"start": v(-123.6, -19.3) * mm, "end": v(-123.6, 7.6) * mm});
            skLineSegment(sketch, "E473", {"start": v(-127.03, -22.01) * mm, "end": v(-127.03, 7.6) * mm});
            skLineSegment(sketch, "E474", {"start": v(-127.03, 7.6) * mm, "end": v(-123.6, 7.6) * mm});
            skLineSegment(sketch, "E475", {"start": v(-127.03, 7.6) * mm, "end": v(-127.03, 60.61) * mm});
            skLineSegment(sketch, "E476", {"start": v(-123.6, 9.59) * mm, "end": v(-124.13, 63.05) * mm});
            skLineSegment(sketch, "E477", {"start": v(-124.13, 63.05) * mm, "end": v(-127.03, 60.61) * mm});
            skLineSegment(sketch, "E478", {"start": v(-123.6, -41.82) * mm, "end": v(-123.6, -38.54) * mm});
            skLineSegment(sketch, "E479", {"start": v(-127.03, -38.54) * mm, "end": v(-123.6, -38.54) * mm});
            skLineSegment(sketch, "E480.bottom", {"start": v(-127.03, -22.01) * mm, "end": v(-123.6, -22.01) * mm});
            skLineSegment(sketch, "E480.left", {"start": v(-127.03, -22.01) * mm, "end": v(-127.03, -38.54) * mm});
            skLineSegment(sketch, "E480.right", {"start": v(-123.6, -22.01) * mm, "end": v(-123.6, -38.54) * mm});
            skSolve(sketch);
        }
        {
            var Q0;
            {var subQ2=sQuery(id+"F2.wireOp",EDGE,"E332");Q0=makeQuery(id+"F2.imprint","IMPRINT",FACE,{"disambiguationData":[TD([[makeQuery(id+"F2.imprint","IMPRINT",EDGE,{"derivedFrom":subQ2}),1.0]])]});}
            var Q1;
            Q1=makeQuery(id+"F2.imprint","IMPRINT",FACE,{"disambiguationData":[TD([[makeQuery(id+"F2.imprint","IMPRINT",EDGE,{"derivedFrom":sQuery(id+"F2.wireOp",EDGE,"E303")}),1.0]])]});
            var Q2;
            Q2=makeQuery(id+"F2.imprint","IMPRINT",FACE,{"disambiguationData":[TD([[makeQuery(id+"F2.imprint","IMPRINT",EDGE,{"derivedFrom":sQuery(id+"F2.wireOp",EDGE,"E302")}),1.0]])]});
            var Q3;
            Q3=makeQuery(id+"F2.imprint","IMPRINT",FACE,{"disambiguationData":[TD([[makeQuery(id+"F2.imprint","IMPRINT",EDGE,{"derivedFrom":sQuery(id+"F2.wireOp",EDGE,"E308")}),1.0]])]});
            var Q4;
            Q4=makeQuery(id+"F2.imprint","IMPRINT",FACE,{"disambiguationData":[TD([[makeQuery(id+"F2.imprint","IMPRINT",EDGE,{"derivedFrom":sQuery(id+"F2.wireOp",EDGE,"E319")}),1.0]])]});
            var Q5;
            Q5=makeQuery(id+"F2.imprint","IMPRINT",FACE,{"disambiguationData":[TD([[makeQuery(id+"F2.imprint","IMPRINT",EDGE,{"derivedFrom":sQuery(id+"F2.wireOp",EDGE,"E312")}),1.0]])]});
            var Q6;
            {var subQ0=sQuery(id+"F2.wireOp",EDGE,"E316");Q6=makeQuery(id+"F2.imprint","IMPRINT",FACE,{"disambiguationData":[TD([[makeQuery(id+"F2.imprint","IMPRINT",EDGE,{"derivedFrom":subQ0}),1.0]])]});}
            var Q7;
            {var subQ0=sQuery(id+"F2.wireOp",EDGE,"E421");Q7=makeQuery(id+"F2.imprint","IMPRINT",FACE,{"disambiguationData":[TD([[makeQuery(id+"F2.imprint","IMPRINT",EDGE,{"derivedFrom":subQ0}),1.0]])]});}
            var Q8;
            Q8=makeQuery(id+"F2.imprint","IMPRINT",FACE,{"disambiguationData":[TD([[makeQuery(id+"F2.imprint","IMPRINT",EDGE,{"derivedFrom":sQuery(id+"F2.wireOp",EDGE,"E396")}),-1.0]])]});
            var Q9;
            {var subQ0=sQuery(id+"F2.wireOp",EDGE,"E434");Q9=makeQuery(id+"F2.imprint","IMPRINT",FACE,{"disambiguationData":[TD([[makeQuery(id+"F2.imprint","IMPRINT",EDGE,{"derivedFrom":subQ0}),-1.0]])]});}
            var Q10;
            {var subQ4=sQuery(id+"F2.wireOp",EDGE,"E346");Q10=makeQuery(id+"F2.imprint","IMPRINT",FACE,{"disambiguationData":[TD([[makeQuery(id+"F2.imprint","IMPRINT",EDGE,{"derivedFrom":subQ4}),-1.0]])]});}
            var Q11;
            Q11=makeQuery(id+"F2.imprint","IMPRINT",FACE,{"disambiguationData":[TD([[makeQuery(id+"F2.imprint","IMPRINT",EDGE,{"derivedFrom":sQuery(id+"F2.wireOp",EDGE,"E322")}),1.0]])]});
            var Q12;
            Q12=makeQuery(id+"F2.imprint","IMPRINT",FACE,{"disambiguationData":[TD([[makeQuery(id+"F2.imprint","IMPRINT",EDGE,{"derivedFrom":sQuery(id+"F2.wireOp",EDGE,"E385")}),1.0]])]});
            var Q13;
            Q13=makeQuery(id+"F2.imprint","IMPRINT",FACE,{"disambiguationData":[TD([[makeQuery(id+"F2.imprint","IMPRINT",EDGE,{"derivedFrom":sQuery(id+"F2.wireOp",EDGE,"E440.top")}),1.0]])]});
            var Q14;
            Q14=makeQuery(id+"F2.imprint","IMPRINT",FACE,{"disambiguationData":[TD([[makeQuery(id+"F2.imprint","IMPRINT",EDGE,{"derivedFrom":sQuery(id+"F2.wireOp",EDGE,"E446")}),1.0]])]});
            var Q15;
            Q15=makeQuery(id+"F2.imprint","IMPRINT",FACE,{"disambiguationData":[TD([[makeQuery(id+"F2.imprint","IMPRINT",EDGE,{"derivedFrom":sQuery(id+"F2.wireOp",EDGE,"E450")}),1.0]])]});
            var Q16;
            Q16=makeQuery(id+"F2.imprint","IMPRINT",FACE,{"disambiguationData":[TD([[makeQuery(id+"F2.imprint","IMPRINT",EDGE,{"derivedFrom":sQuery(id+"F2.wireOp",EDGE,"E389")}),1.0]])]});
            var Q17;
            Q17=makeQuery(id+"F2.imprint","IMPRINT",FACE,{"disambiguationData":[TD([[makeQuery(id+"F2.imprint","IMPRINT",EDGE,{"derivedFrom":sQuery(id+"F2.wireOp",EDGE,"E460")}),1.0]])]});
            var Q18;
            Q18=makeQuery(id+"F2.imprint","IMPRINT",FACE,{"disambiguationData":[TD([[makeQuery(id+"F2.imprint","IMPRINT",EDGE,{"derivedFrom":sQuery(id+"F2.wireOp",EDGE,"E415")}),-1.0]])]});
            var Q19;
            Q19=makeQuery(id+"F2.imprint","IMPRINT",FACE,{"disambiguationData":[TD([[makeQuery(id+"F2.imprint","IMPRINT",EDGE,{"derivedFrom":sQuery(id+"F2.wireOp",EDGE,"E417")}),-1.0]])]});
            var Q20;
            Q20=makeQuery(id+"F2.imprint","IMPRINT",FACE,{"disambiguationData":[TD([[makeQuery(id+"F2.imprint","IMPRINT",EDGE,{"derivedFrom":sQuery(id+"F2.wireOp",EDGE,"E416")}),-1.0]])]});
            var Q21;
            Q21=makeQuery(id+"F2.imprint","IMPRINT",FACE,{"disambiguationData":[TD([[makeQuery(id+"F2.imprint","IMPRINT",EDGE,{"derivedFrom":sQuery(id+"F2.wireOp",EDGE,"E480.bottom")}),-1.0]])]});
            extrude(context, id + "F3", {"entities" : qUnion([Q0, Q1, Q2, Q3, Q4, Q5, Q6, Q7, Q8, Q9, Q10, Q11, Q12, Q13, Q14, Q15, Q16, Q17, Q18, Q19, Q20, Q21]), "operationType" : NewBodyOperationType.ADD, "depth" : 40.64 * mm});
        }
        {
            var Q0;
            Q0=qCreatedBy(makeId("Top.planeOp"),FACE);
            var sketch = newSketch(context, id + "F4", { "sketchPlane" : qUnion([Q0])});
            skLineSegment(sketch, "E481", {"start": v(-215.85, -23.07) * mm, "end": v(-79.78, 113.2) * mm});
            skLineSegment(sketch, "E482", {"start": v(-79.78, 113.2) * mm, "end": v(46.96, 113.2) * mm});
            skLineSegment(sketch, "E483", {"start": v(46.96, 113.2) * mm, "end": v(58.85, 125.1) * mm});
            skLineSegment(sketch, "E484", {"start": v(58.85, 125.1) * mm, "end": v(58.85, 130.59) * mm});
            skLineSegment(sketch, "E485", {"start": v(58.85, 130.59) * mm, "end": v(65.02, 130.59) * mm});
            skLineSegment(sketch, "E486", {"start": v(65.02, 130.59) * mm, "end": v(65.02, 127.13) * mm});
            skLineSegment(sketch, "E487", {"start": v(65.02, 127.13) * mm, "end": v(84.8, 107.35) * mm});
            skLineSegment(sketch, "E488", {"start": v(84.8, 107.35) * mm, "end": v(85.59, 108.14) * mm});
            skLineSegment(sketch, "E489", {"start": v(85.59, 108.14) * mm, "end": v(91.7, 102.02) * mm});
            skLineSegment(sketch, "E490", {"start": v(91.7, 102.02) * mm, "end": v(90.95, 101.28) * mm});
            skLineSegment(sketch, "E491", {"start": v(90.95, 101.28) * mm, "end": v(123.63, 68.6) * mm});
            skLineSegment(sketch, "E492", {"start": v(123.63, 68.6) * mm, "end": v(124.34, 69.31) * mm});
            skLineSegment(sketch, "E493", {"start": v(124.34, 69.31) * mm, "end": v(130.43, 63.22) * mm});
            skLineSegment(sketch, "E494", {"start": v(130.43, 63.22) * mm, "end": v(129.76, 62.54) * mm});
            skLineSegment(sketch, "E495", {"start": v(129.76, 62.54) * mm, "end": v(215.85, -23.56) * mm});
            skLineSegment(sketch, "E496", {"start": v(215.85, -23.56) * mm, "end": v(172.3, -67.15) * mm});
            skLineSegment(sketch, "E497", {"start": v(172.3, -67.15) * mm, "end": v(184.3, -79.94) * mm});
            skLineSegment(sketch, "E498", {"start": v(184.3, -79.94) * mm, "end": v(134.66, -130.59) * mm});
            skLineSegment(sketch, "E499", {"start": v(134.66, -130.59) * mm, "end": v(-126.45, -130.35) * mm});
            skLineSegment(sketch, "E500", {"start": v(-126.45, -130.35) * mm, "end": v(-126.52, -109.63) * mm});
            skLineSegment(sketch, "E501", {"start": v(-126.52, -109.63) * mm, "end": v(-129.44, -109.56) * mm});
            skLineSegment(sketch, "E502", {"start": v(-129.44, -109.56) * mm, "end": v(-132.8, -106.33) * mm});
            skLineSegment(sketch, "E503", {"start": v(-132.8, -106.33) * mm, "end": v(-167.08, -72.04) * mm});
            skLineSegment(sketch, "E504", {"start": v(-167.08, -72.04) * mm, "end": v(-168.6, -70.28) * mm});
            skLineSegment(sketch, "E505", {"start": v(-168.6, -70.28) * mm, "end": v(-215.85, -23.07) * mm});
            skLineSegment(sketch, "E506", {"start": v(-44.13, -19.12) * mm, "end": v(-39.28, -19.12) * mm});
            skLineSegment(sketch, "E507", {"start": v(-39.28, -19.12) * mm, "end": v(-39.28, -23.97) * mm});
            skLineSegment(sketch, "E508", {"start": v(-39.28, -23.97) * mm, "end": v(-44.13, -23.97) * mm});
            skLineSegment(sketch, "E509", {"start": v(-44.13, -23.97) * mm, "end": v(-44.13, -19.12) * mm});
            skLineSegment(sketch, "E510", {"start": v(38.5, 68.25) * mm, "end": v(46.56, 68.25) * mm});
            skLineSegment(sketch, "E511", {"start": v(46.56, 68.25) * mm, "end": v(46.56, 60.2) * mm});
            skLineSegment(sketch, "E512", {"start": v(46.56, 60.2) * mm, "end": v(38.5, 60.2) * mm});
            skLineSegment(sketch, "E513", {"start": v(38.5, 60.2) * mm, "end": v(38.5, 68.25) * mm});
            skLineSegment(sketch, "E514", {"start": v(38.5, -16.41) * mm, "end": v(46.56, -16.41) * mm});
            skLineSegment(sketch, "E515", {"start": v(46.56, -16.41) * mm, "end": v(46.56, -24.48) * mm});
            skLineSegment(sketch, "E516", {"start": v(46.56, -24.48) * mm, "end": v(38.5, -24.48) * mm});
            skLineSegment(sketch, "E517", {"start": v(38.5, -24.48) * mm, "end": v(38.5, -16.41) * mm});
            skLineSegment(sketch, "E518", {"start": v(85.58, 108.14) * mm, "end": v(91.71, 102.01) * mm});
            skLineSegment(sketch, "E519", {"start": v(91.71, 102.01) * mm, "end": v(87.93, 98.22) * mm});
            skLineSegment(sketch, "E520", {"start": v(87.93, 98.22) * mm, "end": v(81.8, 104.35) * mm});
            skLineSegment(sketch, "E521", {"start": v(81.8, 104.35) * mm, "end": v(85.58, 108.14) * mm});
            skLineSegment(sketch, "E522", {"start": v(58.79, 130.55) * mm, "end": v(65.06, 130.55) * mm});
            skLineSegment(sketch, "E523", {"start": v(65.06, 130.55) * mm, "end": v(65.06, 122.85) * mm});
            skLineSegment(sketch, "E524", {"start": v(65.06, 122.85) * mm, "end": v(58.79, 122.85) * mm});
            skLineSegment(sketch, "E525", {"start": v(58.79, 122.85) * mm, "end": v(58.79, 130.55) * mm});
            skLineSegment(sketch, "E526", {"start": v(-43.9, -102.13) * mm, "end": v(-36.5, -102.13) * mm});
            skLineSegment(sketch, "E527", {"start": v(-36.5, -102.13) * mm, "end": v(-36.5, -109.55) * mm});
            skLineSegment(sketch, "E528", {"start": v(-36.5, -109.55) * mm, "end": v(-43.9, -109.55) * mm});
            skLineSegment(sketch, "E529", {"start": v(-43.9, -109.55) * mm, "end": v(-43.9, -102.13) * mm});
            skLineSegment(sketch, "E530", {"start": v(37.92, -102.13) * mm, "end": v(45.33, -102.13) * mm});
            skLineSegment(sketch, "E531", {"start": v(45.33, -102.13) * mm, "end": v(45.33, -109.55) * mm});
            skLineSegment(sketch, "E532", {"start": v(45.33, -109.55) * mm, "end": v(37.92, -109.55) * mm});
            skLineSegment(sketch, "E533", {"start": v(37.92, -109.55) * mm, "end": v(37.92, -102.13) * mm});
            skLineSegment(sketch, "E534", {"start": v(-128, -102.13) * mm, "end": v(-120.6, -102.13) * mm});
            skLineSegment(sketch, "E535", {"start": v(-120.6, -102.13) * mm, "end": v(-120.6, -109.55) * mm});
            skLineSegment(sketch, "E536", {"start": v(-120.6, -109.55) * mm, "end": v(-128, -109.55) * mm});
            skLineSegment(sketch, "E537", {"start": v(-128, -109.55) * mm, "end": v(-128, -102.13) * mm});
            skLineSegment(sketch, "E538", {"start": v(122.45, -18.53) * mm, "end": v(128.43, -18.53) * mm});
            skLineSegment(sketch, "E539", {"start": v(128.43, -18.53) * mm, "end": v(128.43, -24.66) * mm});
            skLineSegment(sketch, "E540", {"start": v(128.43, -24.66) * mm, "end": v(122.45, -24.66) * mm});
            skLineSegment(sketch, "E541", {"start": v(122.45, -24.66) * mm, "end": v(122.45, -18.53) * mm});
            skLineSegment(sketch, "E542", {"start": v(122.45, -102.8) * mm, "end": v(128.43, -102.8) * mm});
            skLineSegment(sketch, "E543", {"start": v(128.43, -102.8) * mm, "end": v(128.43, -108.92) * mm});
            skLineSegment(sketch, "E544", {"start": v(128.43, -108.92) * mm, "end": v(122.45, -108.92) * mm});
            skLineSegment(sketch, "E545", {"start": v(122.45, -108.92) * mm, "end": v(122.45, -102.8) * mm});
            skSolve(sketch);
        }
        {
            var Q0;
            Q0=makeQuery(id+"F4.imprint","IMPRINT",FACE,{"disambiguationData":[TD([[makeQuery(id+"F4.imprint","IMPRINT",EDGE,{"derivedFrom":sQuery(id+"F4.wireOp",EDGE,"E481")}),-1.0]])]});
            extrude(context, id + "F5", {"entities" : qUnion([Q0]), "depth" : 2.54 * mm});
        }
    });
